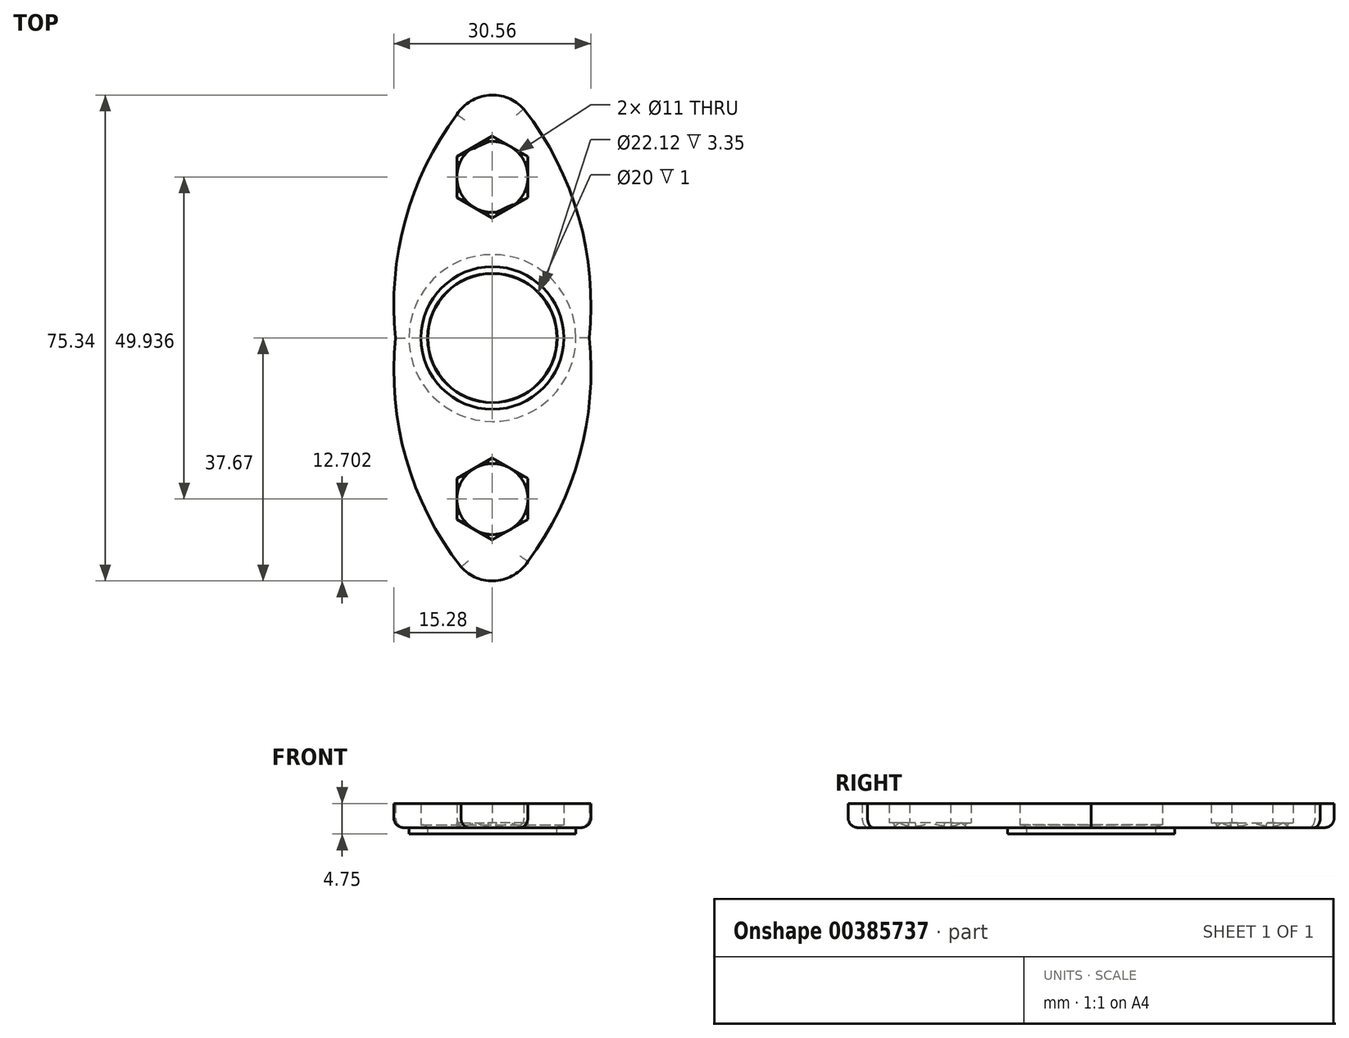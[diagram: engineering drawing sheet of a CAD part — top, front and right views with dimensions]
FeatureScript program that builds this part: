
annotation { "Feature Type Name" : "Feature", "Feature Type Description" : "" }
export const myFeature = defineFeature(function(context is Context, id is Id, definition is map)
    precondition{}
    {
        {
            var Q0;
            Q0=qCreatedBy(makeId("Top.planeOp"),FACE);
            var sketch = newSketch(context, id + "F0", { "sketchPlane" : qUnion([Q0])});
            skCircle(sketch, "E0", {"center": v(0, 0) * mm, "radius": 15 * mm});
            skCircle(sketch, "E1", {"center": v(0, 0) * mm, "radius": 11.06 * mm});
            skArc(sketch, "E2", {"start": v(0, 40.87) * mm, "mid": v(-12.26, 22.18) * mm, "end": v(-15, 0) * mm});
            skArc(sketch, "E3.MirrorCS", {"start": v(0, 40.87) * mm, "mid": v(12.26, 22.18) * mm, "end": v(15, 0) * mm});
            skArc(sketch, "E4.MirrorCS", {"start": v(0, -40.87) * mm, "mid": v(12.26, -22.18) * mm, "end": v(15, 0) * mm});
            skArc(sketch, "E5.MirrorCS", {"start": v(0, -40.87) * mm, "mid": v(-12.26, -22.18) * mm, "end": v(-15, 0) * mm});
            skCircle(sketch, "E6.cCircle", {"center": v(0, 24.97) * mm, "radius": 5.5 * mm, "construction": true});
            skLineSegment(sketch, "E6.0", {"start": v(5.5, 28.14) * mm, "end": v(5.5, 21.8) * mm});
            skLineSegment(sketch, "E6.1", {"start": v(5.5, 21.8) * mm, "end": v(0, 18.62) * mm});
            skLineSegment(sketch, "E6.2", {"start": v(0, 18.62) * mm, "end": v(-5.5, 21.8) * mm});
            skLineSegment(sketch, "E6.3", {"start": v(-5.5, 21.8) * mm, "end": v(-5.5, 28.14) * mm});
            skLineSegment(sketch, "E6.4", {"start": v(-5.5, 28.14) * mm, "end": v(0, 31.32) * mm});
            skLineSegment(sketch, "E6.5", {"start": v(0, 31.32) * mm, "end": v(5.5, 28.14) * mm});
            skPoint(sketch, "E6.0.midPoint", {"position": v(5.5, 24.97) * mm});
            skLineSegment(sketch, "E7.MirrorCS", {"start": v(5.5, -21.8) * mm, "end": v(0, -18.62) * mm});
            skLineSegment(sketch, "E8.MirrorCS", {"start": v(0, -18.62) * mm, "end": v(-5.5, -21.8) * mm});
            skLineSegment(sketch, "E9.MirrorCS", {"start": v(-5.5, -21.8) * mm, "end": v(-5.5, -28.14) * mm});
            skLineSegment(sketch, "E10.MirrorCS", {"start": v(-5.5, -28.14) * mm, "end": v(0, -31.32) * mm});
            skLineSegment(sketch, "E11.MirrorCS", {"start": v(0, -31.32) * mm, "end": v(5.5, -28.14) * mm});
            skCircle(sketch, "E12.MirrorC", {"center": v(0, -24.97) * mm, "radius": 5.5 * mm});
            skLineSegment(sketch, "E13.MirrorCS", {"start": v(5.5, -28.14) * mm, "end": v(5.5, -21.8) * mm});
            skArc(sketch, "E14", {"start": v(-5.5, -34.66) * mm, "mid": v(0, -37.67) * mm, "end": v(5.5, -34.66) * mm});
            skPoint(sketch, "E14.endSnap0", {"position": v(5.5, -24.97) * mm});
            skArc(sketch, "E15.MirrorCS", {"start": v(-5.5, 34.66) * mm, "mid": v(0, 37.67) * mm, "end": v(5.5, 34.66) * mm});
            skSolve(sketch);
        }
        {
            var Q0;
            {var subQ0=sQuery(id+"F0.wireOp",EDGE,"E15.MirrorCS");var subQ1=sQuery(id+"F0.wireOp",EDGE,"E2");var subQ2=makeQuery(id+"F0.imprint","INTERSECT",VERTEX,{"disambiguationData":[OD(0.0)],"derivedFrom":[subQ1,subQ0]});Q0=makeQuery(id+"F0.imprint","IMPRINT",FACE,{"disambiguationData":[TD([[makeQuery(id+"F0.imprint","IMPRINT",EDGE,{"disambiguationData":[TD([[subQ2,1.0]])],"derivedFrom":subQ1}),-1.0]])]});}
            var Q1;
            {var subQ0=sQuery(id+"F0.wireOp",EDGE,"E15.MirrorCS");var subQ1=sQuery(id+"F0.wireOp",EDGE,"E3.MirrorCS");var subQ2=makeQuery(id+"F0.imprint","INTERSECT",VERTEX,{"disambiguationData":[OD(0.0)],"derivedFrom":[subQ1,subQ0]});Q1=makeQuery(id+"F0.imprint","IMPRINT",FACE,{"disambiguationData":[TD([[makeQuery(id+"F0.imprint","IMPRINT",EDGE,{"disambiguationData":[TD([[subQ2,1.0]])],"derivedFrom":subQ1}),1.0]])]});}
            var Q2;
            {var subQ0=sQuery(id+"F0.wireOp",EDGE,"E14");var subQ1=sQuery(id+"F0.wireOp",EDGE,"E4.MirrorCS");var subQ2=makeQuery(id+"F0.imprint","INTERSECT",VERTEX,{"disambiguationData":[OD(0.0)],"derivedFrom":[subQ1,subQ0]});Q2=makeQuery(id+"F0.imprint","IMPRINT",FACE,{"disambiguationData":[TD([[makeQuery(id+"F0.imprint","IMPRINT",EDGE,{"disambiguationData":[TD([[subQ2,1.0]])],"derivedFrom":subQ1}),-1.0]])]});}
            var Q3;
            {var subQ0=sQuery(id+"F0.wireOp",EDGE,"E14");var subQ1=sQuery(id+"F0.wireOp",EDGE,"E5.MirrorCS");var subQ2=makeQuery(id+"F0.imprint","INTERSECT",VERTEX,{"disambiguationData":[OD(0.0)],"derivedFrom":[subQ1,subQ0]});Q3=makeQuery(id+"F0.imprint","IMPRINT",FACE,{"disambiguationData":[TD([[makeQuery(id+"F0.imprint","IMPRINT",EDGE,{"disambiguationData":[TD([[subQ2,1.0]])],"derivedFrom":subQ1}),1.0]])]});}
            var Q4;
            Q4=makeQuery(id+"F0.imprint","IMPRINT",FACE,{"disambiguationData":[TD([[makeQuery(id+"F0.imprint","IMPRINT",EDGE,{"derivedFrom":sQuery(id+"F0.wireOp",EDGE,"E1")}),-1.0]])]});
            var Q5;
            Q5=makeQuery(id+"F0.imprint","IMPRINT",FACE,{"disambiguationData":[TD([[makeQuery(id+"F0.imprint","IMPRINT",EDGE,{"derivedFrom":sQuery(id+"F0.wireOp",EDGE,"E6.0")}),1.0]])]});
            var Q6;
            Q6=makeQuery(id+"F0.imprint","IMPRINT",FACE,{"disambiguationData":[TD([[makeQuery(id+"F0.imprint","IMPRINT",EDGE,{"derivedFrom":sQuery(id+"F0.wireOp",EDGE,"E7.MirrorCS")}),-1.0]])]});
            extrude(context, id + "F1", {"entities" : qUnion([Q0, Q1, Q2, Q3, Q4, Q5, Q6]), "depth" : 3.75 * mm});
        }
        {
            var Q0;
            Q0=makeQuery(id+"F1.opExtrude","CAP_FACE",FACE,{"disambiguationData":[OSD([sQuery(id+"F0.wireOp",EDGE,"E1"),sQuery(id+"F0.wireOp",EDGE,"E2"),sQuery(id+"F0.wireOp",EDGE,"E3.MirrorCS"),sQuery(id+"F0.wireOp",EDGE,"E4.MirrorCS"),sQuery(id+"F0.wireOp",EDGE,"E5.MirrorCS"),sQuery(id+"F0.wireOp",EDGE,"E6.0"),sQuery(id+"F0.wireOp",EDGE,"E6.1"),sQuery(id+"F0.wireOp",EDGE,"E6.2"),sQuery(id+"F0.wireOp",EDGE,"E6.3"),sQuery(id+"F0.wireOp",EDGE,"E6.4"),sQuery(id+"F0.wireOp",EDGE,"E6.5"),sQuery(id+"F0.wireOp",EDGE,"E7.MirrorCS"),sQuery(id+"F0.wireOp",EDGE,"E8.MirrorCS"),sQuery(id+"F0.wireOp",EDGE,"E9.MirrorCS"),sQuery(id+"F0.wireOp",EDGE,"E10.MirrorCS"),sQuery(id+"F0.wireOp",EDGE,"E11.MirrorCS"),sQuery(id+"F0.wireOp",EDGE,"E13.MirrorCS"),sQuery(id+"F0.wireOp",EDGE,"E14"),sQuery(id+"F0.wireOp",EDGE,"E15.MirrorCS")])],"isStart":true});
            var sketch = newSketch(context, id + "F2", { "sketchPlane" : qUnion([Q0])});
            skCircle(sketch, "E16", {"center": v(0, 0) * mm, "radius": 12.94 * mm});
            skCircle(sketch, "E17", {"center": v(0, 0) * mm, "radius": 10 * mm});
            skSolve(sketch);
        }
        {
            var Q0;
            Q0 = qSketchRegion(id + "F2", true);
            extrude(context, id + "F3", {"entities" : qUnion([Q0]), "operationType" : NewBodyOperationType.ADD, "depth" : 1 * mm});
        }
        {
            var Q0;
            Q0=makeQuery(id+"F1.opExtrude","CAP_FACE",FACE,{"disambiguationData":[OSD([sQuery(id+"F0.wireOp",EDGE,"E1"),sQuery(id+"F0.wireOp",EDGE,"E2"),sQuery(id+"F0.wireOp",EDGE,"E3.MirrorCS"),sQuery(id+"F0.wireOp",EDGE,"E4.MirrorCS"),sQuery(id+"F0.wireOp",EDGE,"E5.MirrorCS"),sQuery(id+"F0.wireOp",EDGE,"E6.0"),sQuery(id+"F0.wireOp",EDGE,"E6.1"),sQuery(id+"F0.wireOp",EDGE,"E6.2"),sQuery(id+"F0.wireOp",EDGE,"E6.3"),sQuery(id+"F0.wireOp",EDGE,"E6.4"),sQuery(id+"F0.wireOp",EDGE,"E6.5"),sQuery(id+"F0.wireOp",EDGE,"E7.MirrorCS"),sQuery(id+"F0.wireOp",EDGE,"E8.MirrorCS"),sQuery(id+"F0.wireOp",EDGE,"E9.MirrorCS"),sQuery(id+"F0.wireOp",EDGE,"E10.MirrorCS"),sQuery(id+"F0.wireOp",EDGE,"E11.MirrorCS"),sQuery(id+"F0.wireOp",EDGE,"E13.MirrorCS"),sQuery(id+"F0.wireOp",EDGE,"E14"),sQuery(id+"F0.wireOp",EDGE,"E15.MirrorCS")])],"isStart":true});
            var sketch = newSketch(context, id + "F4", { "sketchPlane" : qUnion([Q0])});
            skCircle(sketch, "E18", {"center": v(0, 0) * mm, "radius": 12.92 * mm});
            skCircle(sketch, "E19", {"center": v(0, 0) * mm, "radius": 10.04 * mm});
            skSolve(sketch);
        }
        {
            var Q0;
            Q0 = qSketchRegion(id + "F4", true);
            extrude(context, id + "F5", {"entities" : qUnion([Q0]), "operationType" : NewBodyOperationType.ADD, "oppositeDirection" : true, "depth" : 0.4 * mm});
        }
        {
            var Q0;
            Q0=makeQuery(id+"F5.opExtrude","CAP_EDGE",EDGE,{"disambiguationData":[OSD([sQuery(id+"F4.wireOp",EDGE,"E19")])],"isStart":false});
            fillet(context, id + "F6", {"entities" : qUnion([Q0]), "radius" : 1 * mm, "tangentPropagation" : true, "allowEdgeOverflow" : false});
        }
        {
            var Q0;
            Q0=makeQuery(id+"F1.opExtrude","CAP_FACE",FACE,{"disambiguationData":[OSD([sQuery(id+"F0.wireOp",EDGE,"E1"),sQuery(id+"F0.wireOp",EDGE,"E2"),sQuery(id+"F0.wireOp",EDGE,"E3.MirrorCS"),sQuery(id+"F0.wireOp",EDGE,"E4.MirrorCS"),sQuery(id+"F0.wireOp",EDGE,"E5.MirrorCS"),sQuery(id+"F0.wireOp",EDGE,"E6.0"),sQuery(id+"F0.wireOp",EDGE,"E6.1"),sQuery(id+"F0.wireOp",EDGE,"E6.2"),sQuery(id+"F0.wireOp",EDGE,"E6.3"),sQuery(id+"F0.wireOp",EDGE,"E6.4"),sQuery(id+"F0.wireOp",EDGE,"E6.5"),sQuery(id+"F0.wireOp",EDGE,"E7.MirrorCS"),sQuery(id+"F0.wireOp",EDGE,"E8.MirrorCS"),sQuery(id+"F0.wireOp",EDGE,"E9.MirrorCS"),sQuery(id+"F0.wireOp",EDGE,"E10.MirrorCS"),sQuery(id+"F0.wireOp",EDGE,"E11.MirrorCS"),sQuery(id+"F0.wireOp",EDGE,"E13.MirrorCS"),sQuery(id+"F0.wireOp",EDGE,"E14"),sQuery(id+"F0.wireOp",EDGE,"E15.MirrorCS")])],"isStart":true});
            var sketch = newSketch(context, id + "F7", { "sketchPlane" : qUnion([Q0])});
            skCircle(sketch, "E20", {"center": v(0, 24.97) * mm, "radius": 5.5 * mm});
            skPoint(sketch, "E20.centerSnap0", {"position": v(5.5, 24.97) * mm});
            skCircle(sketch, "E21", {"center": v(0, 24.97) * mm, "radius": 7.05 * mm});
            skCircle(sketch, "E22.MirrorC", {"center": v(0, -24.97) * mm, "radius": 5.5 * mm});
            skCircle(sketch, "E23.MirrorC", {"center": v(0, -24.97) * mm, "radius": 7.05 * mm});
            skSolve(sketch);
        }
        {
            var Q0;
            Q0 = qSketchRegion(id + "F7", true);
            extrude(context, id + "F8", {"entities" : qUnion([Q0]), "operationType" : NewBodyOperationType.ADD, "oppositeDirection" : true, "depth" : 0.75 * mm});
        }
        {
            var Q0;
            {var subQ0=sQuery(id+"F7.wireOp",EDGE,"E20");Q0=makeQuery(id+"F8.boolean.opBoolean","SPLIT",EDGE,{"disambiguationData":[TD([makeQuery(id+"F1.opExtrude","SWEPT_FACE",FACE,{"disambiguationData":[OSD([sQuery(id+"F0.wireOp",EDGE,"E8.MirrorCS")])]}),makeQuery(id+"F1.opExtrude","SWEPT_FACE",FACE,{"disambiguationData":[OSD([sQuery(id+"F0.wireOp",EDGE,"E9.MirrorCS")])]}),makeQuery(id+"F8.opExtrude","SWEPT_FACE",FACE,{"disambiguationData":[OSD([subQ0])]}),makeQuery(id+"F8.opExtrude","CAP_FACE",FACE,{"disambiguationData":[OSD([subQ0,sQuery(id+"F7.wireOp",EDGE,"E21")])],"isStart":false})])],"derivedFrom":makeQuery(id+"F8.opExtrude","CAP_EDGE",EDGE,{"disambiguationData":[OSD([subQ0])],"isStart":false})});}
            var Q1;
            {var subQ0=sQuery(id+"F7.wireOp",EDGE,"E20");Q1=makeQuery(id+"F8.boolean.opBoolean","SPLIT",EDGE,{"disambiguationData":[TD([makeQuery(id+"F1.opExtrude","SWEPT_FACE",FACE,{"disambiguationData":[OSD([sQuery(id+"F0.wireOp",EDGE,"E9.MirrorCS")])]}),makeQuery(id+"F1.opExtrude","SWEPT_FACE",FACE,{"disambiguationData":[OSD([sQuery(id+"F0.wireOp",EDGE,"E10.MirrorCS")])]}),makeQuery(id+"F8.opExtrude","SWEPT_FACE",FACE,{"disambiguationData":[OSD([subQ0])]}),makeQuery(id+"F8.opExtrude","CAP_FACE",FACE,{"disambiguationData":[OSD([subQ0,sQuery(id+"F7.wireOp",EDGE,"E21")])],"isStart":false})])],"derivedFrom":makeQuery(id+"F8.opExtrude","CAP_EDGE",EDGE,{"disambiguationData":[OSD([subQ0])],"isStart":false})});}
            var Q2;
            {var subQ0=sQuery(id+"F7.wireOp",EDGE,"E20");Q2=makeQuery(id+"F8.boolean.opBoolean","SPLIT",EDGE,{"disambiguationData":[TD([makeQuery(id+"F1.opExtrude","SWEPT_FACE",FACE,{"disambiguationData":[OSD([sQuery(id+"F0.wireOp",EDGE,"E7.MirrorCS")])]}),makeQuery(id+"F1.opExtrude","SWEPT_FACE",FACE,{"disambiguationData":[OSD([sQuery(id+"F0.wireOp",EDGE,"E8.MirrorCS")])]}),makeQuery(id+"F8.opExtrude","SWEPT_FACE",FACE,{"disambiguationData":[OSD([subQ0])]}),makeQuery(id+"F8.opExtrude","CAP_FACE",FACE,{"disambiguationData":[OSD([subQ0,sQuery(id+"F7.wireOp",EDGE,"E21")])],"isStart":false})])],"derivedFrom":makeQuery(id+"F8.opExtrude","CAP_EDGE",EDGE,{"disambiguationData":[OSD([subQ0])],"isStart":false})});}
            var Q3;
            {var subQ0=sQuery(id+"F7.wireOp",EDGE,"E20");Q3=makeQuery(id+"F8.boolean.opBoolean","SPLIT",EDGE,{"disambiguationData":[TD([makeQuery(id+"F1.opExtrude","SWEPT_FACE",FACE,{"disambiguationData":[OSD([sQuery(id+"F0.wireOp",EDGE,"E7.MirrorCS")])]}),makeQuery(id+"F1.opExtrude","SWEPT_FACE",FACE,{"disambiguationData":[OSD([sQuery(id+"F0.wireOp",EDGE,"E13.MirrorCS")])]}),makeQuery(id+"F8.opExtrude","SWEPT_FACE",FACE,{"disambiguationData":[OSD([subQ0])]}),makeQuery(id+"F8.opExtrude","CAP_FACE",FACE,{"disambiguationData":[OSD([subQ0,sQuery(id+"F7.wireOp",EDGE,"E21")])],"isStart":false})])],"derivedFrom":makeQuery(id+"F8.opExtrude","CAP_EDGE",EDGE,{"disambiguationData":[OSD([subQ0])],"isStart":false})});}
            var Q4;
            {var subQ0=sQuery(id+"F7.wireOp",EDGE,"E20");Q4=makeQuery(id+"F8.boolean.opBoolean","SPLIT",EDGE,{"disambiguationData":[TD([makeQuery(id+"F1.opExtrude","SWEPT_FACE",FACE,{"disambiguationData":[OSD([sQuery(id+"F0.wireOp",EDGE,"E10.MirrorCS")])]}),makeQuery(id+"F1.opExtrude","SWEPT_FACE",FACE,{"disambiguationData":[OSD([sQuery(id+"F0.wireOp",EDGE,"E11.MirrorCS")])]}),makeQuery(id+"F8.opExtrude","SWEPT_FACE",FACE,{"disambiguationData":[OSD([subQ0])]}),makeQuery(id+"F8.opExtrude","CAP_FACE",FACE,{"disambiguationData":[OSD([subQ0,sQuery(id+"F7.wireOp",EDGE,"E21")])],"isStart":false})])],"derivedFrom":makeQuery(id+"F8.opExtrude","CAP_EDGE",EDGE,{"disambiguationData":[OSD([subQ0])],"isStart":false})});}
            fillet(context, id + "F9", {"entities" : qUnion([Q0, Q1, Q2, Q3, Q4]), "radius" : 0.5 * mm, "tangentPropagation" : true, "allowEdgeOverflow" : false});
        }
        {
            var Q0;
            {var subQ0=sQuery(id+"F7.wireOp",EDGE,"E22.MirrorC");Q0=makeQuery(id+"F8.boolean.opBoolean","SPLIT",EDGE,{"disambiguationData":[TD([makeQuery(id+"F1.opExtrude","SWEPT_FACE",FACE,{"disambiguationData":[OSD([sQuery(id+"F0.wireOp",EDGE,"E6.2")])]}),makeQuery(id+"F1.opExtrude","SWEPT_FACE",FACE,{"disambiguationData":[OSD([sQuery(id+"F0.wireOp",EDGE,"E6.3")])]}),makeQuery(id+"F8.opExtrude","SWEPT_FACE",FACE,{"disambiguationData":[OSD([subQ0])]}),makeQuery(id+"F8.opExtrude","CAP_FACE",FACE,{"disambiguationData":[OSD([subQ0,sQuery(id+"F7.wireOp",EDGE,"E23.MirrorC")])],"isStart":false})])],"derivedFrom":makeQuery(id+"F8.opExtrude","CAP_EDGE",EDGE,{"disambiguationData":[OSD([subQ0])],"isStart":false})});}
            var Q1;
            {var subQ0=sQuery(id+"F7.wireOp",EDGE,"E22.MirrorC");Q1=makeQuery(id+"F8.boolean.opBoolean","SPLIT",EDGE,{"disambiguationData":[TD([makeQuery(id+"F1.opExtrude","SWEPT_FACE",FACE,{"disambiguationData":[OSD([sQuery(id+"F0.wireOp",EDGE,"E6.3")])]}),makeQuery(id+"F1.opExtrude","SWEPT_FACE",FACE,{"disambiguationData":[OSD([sQuery(id+"F0.wireOp",EDGE,"E6.4")])]}),makeQuery(id+"F8.opExtrude","SWEPT_FACE",FACE,{"disambiguationData":[OSD([subQ0])]}),makeQuery(id+"F8.opExtrude","CAP_FACE",FACE,{"disambiguationData":[OSD([subQ0,sQuery(id+"F7.wireOp",EDGE,"E23.MirrorC")])],"isStart":false})])],"derivedFrom":makeQuery(id+"F8.opExtrude","CAP_EDGE",EDGE,{"disambiguationData":[OSD([subQ0])],"isStart":false})});}
            var Q2;
            {var subQ0=sQuery(id+"F7.wireOp",EDGE,"E22.MirrorC");Q2=makeQuery(id+"F8.boolean.opBoolean","SPLIT",EDGE,{"disambiguationData":[TD([makeQuery(id+"F1.opExtrude","SWEPT_FACE",FACE,{"disambiguationData":[OSD([sQuery(id+"F0.wireOp",EDGE,"E6.4")])]}),makeQuery(id+"F1.opExtrude","SWEPT_FACE",FACE,{"disambiguationData":[OSD([sQuery(id+"F0.wireOp",EDGE,"E6.5")])]}),makeQuery(id+"F8.opExtrude","SWEPT_FACE",FACE,{"disambiguationData":[OSD([subQ0])]}),makeQuery(id+"F8.opExtrude","CAP_FACE",FACE,{"disambiguationData":[OSD([subQ0,sQuery(id+"F7.wireOp",EDGE,"E23.MirrorC")])],"isStart":false})])],"derivedFrom":makeQuery(id+"F8.opExtrude","CAP_EDGE",EDGE,{"disambiguationData":[OSD([subQ0])],"isStart":false})});}
            var Q3;
            {var subQ0=sQuery(id+"F7.wireOp",EDGE,"E22.MirrorC");Q3=makeQuery(id+"F8.boolean.opBoolean","SPLIT",EDGE,{"disambiguationData":[TD([makeQuery(id+"F1.opExtrude","SWEPT_FACE",FACE,{"disambiguationData":[OSD([sQuery(id+"F0.wireOp",EDGE,"E6.0")])]}),makeQuery(id+"F1.opExtrude","SWEPT_FACE",FACE,{"disambiguationData":[OSD([sQuery(id+"F0.wireOp",EDGE,"E6.5")])]}),makeQuery(id+"F8.opExtrude","SWEPT_FACE",FACE,{"disambiguationData":[OSD([subQ0])]}),makeQuery(id+"F8.opExtrude","CAP_FACE",FACE,{"disambiguationData":[OSD([subQ0,sQuery(id+"F7.wireOp",EDGE,"E23.MirrorC")])],"isStart":false})])],"derivedFrom":makeQuery(id+"F8.opExtrude","CAP_EDGE",EDGE,{"disambiguationData":[OSD([subQ0])],"isStart":false})});}
            var Q4;
            {var subQ0=sQuery(id+"F7.wireOp",EDGE,"E22.MirrorC");Q4=makeQuery(id+"F8.boolean.opBoolean","SPLIT",EDGE,{"disambiguationData":[TD([makeQuery(id+"F1.opExtrude","SWEPT_FACE",FACE,{"disambiguationData":[OSD([sQuery(id+"F0.wireOp",EDGE,"E6.0")])]}),makeQuery(id+"F1.opExtrude","SWEPT_FACE",FACE,{"disambiguationData":[OSD([sQuery(id+"F0.wireOp",EDGE,"E6.1")])]}),makeQuery(id+"F8.opExtrude","SWEPT_FACE",FACE,{"disambiguationData":[OSD([subQ0])]}),makeQuery(id+"F8.opExtrude","CAP_FACE",FACE,{"disambiguationData":[OSD([subQ0,sQuery(id+"F7.wireOp",EDGE,"E23.MirrorC")])],"isStart":false})])],"derivedFrom":makeQuery(id+"F8.opExtrude","CAP_EDGE",EDGE,{"disambiguationData":[OSD([subQ0])],"isStart":false})});}
            var Q5;
            {var subQ0=sQuery(id+"F7.wireOp",EDGE,"E22.MirrorC");Q5=makeQuery(id+"F8.boolean.opBoolean","SPLIT",EDGE,{"disambiguationData":[TD([makeQuery(id+"F1.opExtrude","SWEPT_FACE",FACE,{"disambiguationData":[OSD([sQuery(id+"F0.wireOp",EDGE,"E6.1")])]}),makeQuery(id+"F1.opExtrude","SWEPT_FACE",FACE,{"disambiguationData":[OSD([sQuery(id+"F0.wireOp",EDGE,"E6.2")])]}),makeQuery(id+"F8.opExtrude","SWEPT_FACE",FACE,{"disambiguationData":[OSD([subQ0])]}),makeQuery(id+"F8.opExtrude","CAP_FACE",FACE,{"disambiguationData":[OSD([subQ0,sQuery(id+"F7.wireOp",EDGE,"E23.MirrorC")])],"isStart":false})])],"derivedFrom":makeQuery(id+"F8.opExtrude","CAP_EDGE",EDGE,{"disambiguationData":[OSD([subQ0])],"isStart":false})});}
            fillet(context, id + "F10", {"entities" : qUnion([Q0, Q1, Q2, Q3, Q4, Q5]), "radius" : 0.5 * mm, "tangentPropagation" : true, "allowEdgeOverflow" : false});
        }
        {
            var Q0;
            Q0=makeQuery(id+"F1.opExtrude","CAP_EDGE",EDGE,{"disambiguationData":[OSD([sQuery(id+"F0.wireOp",EDGE,"E4.MirrorCS")])],"isStart":true});
            var Q1;
            Q1=makeQuery(id+"F1.opExtrude","CAP_EDGE",EDGE,{"disambiguationData":[OSD([sQuery(id+"F0.wireOp",EDGE,"E3.MirrorCS")])],"isStart":true});
            var Q2;
            Q2=makeQuery(id+"F1.opExtrude","CAP_EDGE",EDGE,{"disambiguationData":[OSD([sQuery(id+"F0.wireOp",EDGE,"E15.MirrorCS")])],"isStart":true});
            var Q3;
            Q3=makeQuery(id+"F1.opExtrude","CAP_EDGE",EDGE,{"disambiguationData":[OSD([sQuery(id+"F0.wireOp",EDGE,"E2")])],"isStart":true});
            var Q4;
            Q4=makeQuery(id+"F1.opExtrude","CAP_EDGE",EDGE,{"disambiguationData":[OSD([sQuery(id+"F0.wireOp",EDGE,"E5.MirrorCS")])],"isStart":true});
            var Q5;
            Q5=makeQuery(id+"F1.opExtrude","CAP_EDGE",EDGE,{"disambiguationData":[OSD([sQuery(id+"F0.wireOp",EDGE,"E14")])],"isStart":true});
            fillet(context, id + "F11", {"entities" : qUnion([Q0, Q1, Q2, Q3, Q4, Q5]), "radius" : 1.5 * mm, "tangentPropagation" : true, "allowEdgeOverflow" : false});
        }
    });
